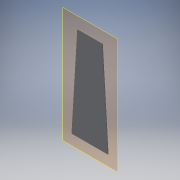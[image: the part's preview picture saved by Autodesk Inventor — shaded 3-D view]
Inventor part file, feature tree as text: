
AUTODESK INVENTOR PART (.ipt)
format: ipt  version: 2019.2 (Build 232265000, 265)  size: 119,296 bytes
history: native  units: in
note: dims shown in document units (in); Inventor stores cm internally (conversion verified against a paired STEP export)
features: other x3, sketch x2, plane x1, extrude x1, chamfer x1, hole x1
ambient origin geometry x8: Origin, YZ Plane, XZ Plane, XY Plane, X Axis, Y Axis, Z Axis, Center Point
bodies: Solid1 (feature_tree)
feature tree (9):
  plane  "Work Plane1"
  extrude  "Extrusion1"  Depth=0.0787in
  chamfer  "Chamfer1"  Distance=0.0787in Angle=45.0deg
  hole  "Hole1"  [1 undecoded]
  sketch  "Sketch1"  dims[d0=0.0787in d1=0.0in d2=0.0394in d3=0.0394in d4=0.0787in d5=45.0deg]
  sketch  "Sketch2"  dims[d6=0.2362in d7=0.2362in d8=0.1575in d9=0.2362in d10=0.1575in d11=0.0787in d12=90.0deg d13=0.315in d14=0.8108in]
  other  "<userpath>\Desktop\3dprojects\OpenEmoto\MainFrame\Battery\Assembly.iam"
  other  "Assembly.iam"
  other  "LowerCage:1"
note: 1 required parameter value undecoded (feature->parameter linkage not recoverable at this tier; creation-order binding heuristic only, values carry confidence <= 0.55)
